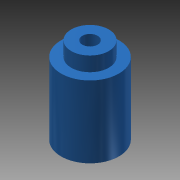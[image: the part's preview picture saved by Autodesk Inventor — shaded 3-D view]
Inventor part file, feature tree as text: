
AUTODESK INVENTOR PART (.ipt)
format: ipt  version: 2013 (Build 170138000, 138)  size: 87,552 bytes
history: native  units: mm
features: extrude x2, sketch x2
ambient origin geometry x8: Origin, YZ Plane, XZ Plane, XY Plane, X Axis, Y Axis, Z Axis, Center Point
bodies: Solid1 (feature_tree)
feature tree (4):
  extrude  "Extrusion1"  Depth=12.0mm
  extrude  "Extrusion2"  Depth=7.8mm
  sketch  "Sketch1"  dims[d0=3.2mm d1=12.0mm]
  sketch  "Sketch2"  dims[d2=14.9mm d3=0.0mm d4=7.8mm d5=3.0mm d6=0.0mm]
